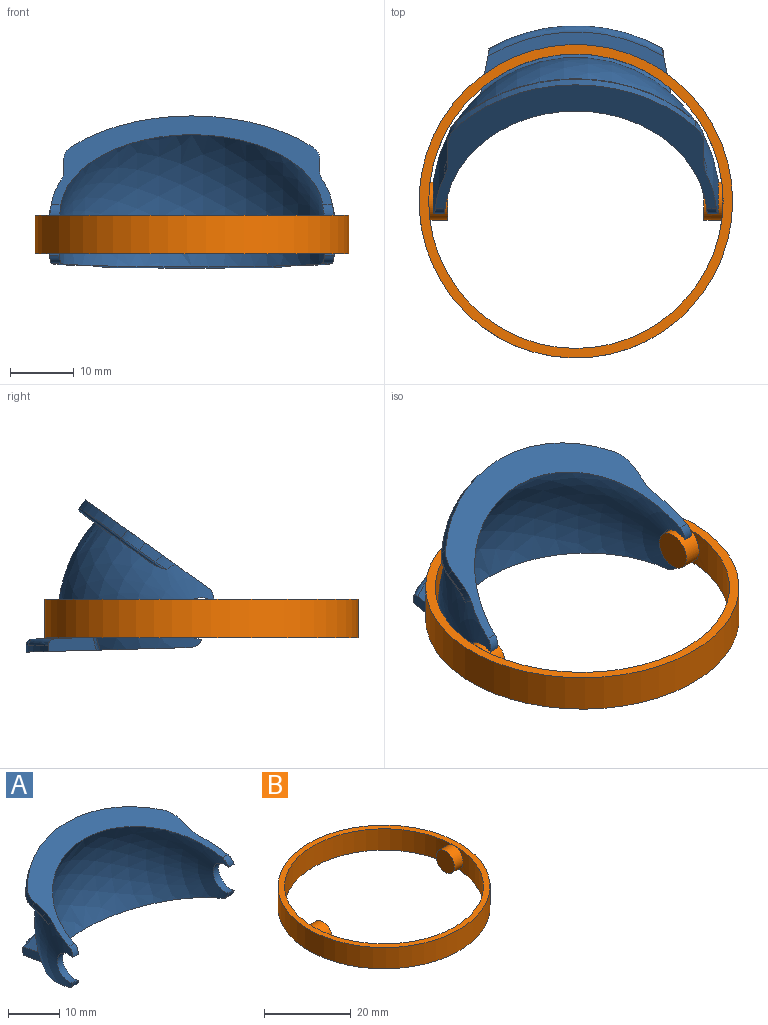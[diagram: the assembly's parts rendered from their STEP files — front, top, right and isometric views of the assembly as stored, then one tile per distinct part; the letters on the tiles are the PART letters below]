
ASSEMBLY  parts=2 mates=1
PART A: 33 faces, bbox 44.9x34.7x45.3 mm
  f0: sphere r=22.5mm, area 1052.7mm2, adj f2,f3,f7,f10,f11,f16,f17,f18
  f1: sphere r=21mm, area 1121.9mm2, adj f2,f3,f27,f28,f29,f30,f31,f32
  f2: plane 43.94x24.36mm, normal (0,-0.32,-0.95), area 263.8mm2, adj f0,f1,f12,f13,f14,f16,f17,f29
  f3: plane 44.02x22.54mm, normal (0,-0.32,0.95), area 263mm2, adj f0,f1,f4,f5,f6,f8,f9,f10
  f4: plane 3.8x2.37mm, normal (1,0,0), area 4.8mm2, adj f3,f8,f10,f21
  f5: cylinder r=25.55mm len=37.3mm, axis (0,-0.32,0.95), area 62.7mm2, adj f3,f8,f9,f23
  f6: plane 3.8x2.37mm, normal (-1,0,0), area 4.8mm2, adj f3,f9,f11,f25
  f7: plane 39x13.37mm, normal (0,0.32,-0.95), area 122.5mm2, adj f0,f20,f21,f22,f23,f24,f25,f26
  f8: cylinder r=5mm len=3.72mm, axis (0,-0.32,0.95), area 5.6mm2, adj f3,f4,f5,f22
  f9: cylinder r=5mm len=3.72mm, axis (0,-0.32,0.95), area 5.6mm2, adj f3,f5,f6,f24
  f10: torus R=11.46mm, axis (-1,0,0), area 3.4mm2, adj f0,f3,f4,f20
  f11: torus R=11.46mm, axis (-1,0,0), area 3.4mm2, adj f0,f3,f6,f26
  f12: plane 7.81x4.87mm, normal (-0.98,0.18,-0.06), area 14.6mm2, adj f2,f14,f15,f16,f18,f19
  f13: plane 7.81x4.87mm, normal (0.98,0.18,-0.06), area 14.6mm2, adj f2,f14,f15,f17,f18,f19
  f14: cylinder r=27.55mm len=26.99mm, axis (0,-0.32,-0.95), area 28.2mm2, adj f2,f12,f13,f19
  f15: plane 29.15x7.75mm, normal (0,0.32,0.95), area 93.1mm2, adj f12,f13,f18,f19
  f16: torus R=14.14mm, axis (-0.98,0.18,-0.06), area 1.8mm2, adj f0,f2,f12,f18
  f17: torus R=14.14mm, axis (-0.98,-0.18,0.06), area 1.8mm2, adj f0,f2,f13,f18
  f18: torus R=23.45mm, axis (0,-0.32,-0.95), area 52.6mm2, adj f0,f12,f13,f15,f16,f17
  f19: torus R=26.55mm, axis (0,-0.32,-0.95), area 45.1mm2, adj f12,f13,f14,f15
  f20: bspline ~3.37x1.59mm, area 0.9mm2, adj f0,f7,f10,f21
  f21: cylinder r=0.5mm len=2.99mm, axis (0,-0.95,-0.32), area 2.3mm2, adj f4,f7,f20,f22
  f22: torus R=4.5mm, axis (0,-0.32,0.95), area 2.8mm2, adj f7,f8,f21,f23
  f23: torus R=25.05mm, axis (0,-0.32,0.95), area 32.6mm2, adj f5,f7,f22,f24
  f24: torus R=4.5mm, axis (0,-0.32,0.95), area 2.8mm2, adj f7,f9,f23,f25
  f25: cylinder r=0.5mm len=2.99mm, axis (0,0.95,0.32), area 2.3mm2, adj f6,f7,f24,f26
  f26: bspline ~3.37x1.59mm, area 0.9mm2, adj f0,f7,f11,f25
  f27: cylinder r=3.25mm len=6.5mm, axis (1,0,0), area 18.7mm2, adj f0,f1,f29,f30
  f28: cylinder r=3.25mm len=6.5mm, axis (1,0,0), area 18.7mm2, adj f0,f1,f31,f32
  f29: cylinder r=2mm len=1.84mm, axis (1,0,0), area 3.6mm2, adj f0,f1,f2,f27
  f30: cylinder r=2mm len=1.84mm, axis (1,0,0), area 3.6mm2, adj f0,f1,f3,f27
  f31: cylinder r=2mm len=1.84mm, axis (1,0,0), area 3.6mm2, adj f0,f1,f2,f28
  f32: cylinder r=2mm len=1.84mm, axis (1,0,0), area 3.6mm2, adj f0,f1,f3,f28
PART B: 9 faces, bbox 49x49x6 mm
  f0: cylinder r=23mm len=46mm, axis (0,0,-1), area 405.2mm2, adj f3,f4,f5,f6
  f1: cylinder r=23mm len=46mm, axis (0,0,-1), area 405.2mm2, adj f3,f4,f5,f6
  f2: cylinder r=24.5mm len=49mm, axis (0,0,-1), area 923.6mm2, adj f3,f4
  f3: plane 49x49mm, normal (0,0,1), area 223.8mm2, adj f0,f1,f2
  f4: plane 49x49mm, normal (0,0,-1), area 223.8mm2, adj f0,f1,f2
  f5: cylinder r=3mm len=6mm, axis (-1,0,0), area 54.7mm2, adj f0,f1,f8
  f6: cylinder r=3mm len=6mm, axis (1,0,0), area 54.7mm2, adj f0,f1,f7
  f7: plane 6x6mm, normal (1,0,0), area 28.3mm2, adj f6
  f8: plane 6x6mm, normal (-1,0,0), area 28.3mm2, adj f5
PLACE A rot(axis=(1,0,0),17deg) t=(0.33,1.11,12.36)mm
PLACE B t=(0.34,1.11,12.36)mm fixed
MATE revolute A.f27 <-> B.f5  axis (1,0,0) through (-21.17,1.11,12.36)mm
